# Revit family: Legrand Linkeo coffrets fixes avec panneaux latéraux fixes
name_source: partatom
category: Equipement spécialisé
units: mm (PartAtom-declared; Revit-internal decimal feet)

## family parameters
Basée sur le plan de construction = Non
Cote de connecteur circulaire = Utiliser le diamètre
Couper avec des vides une fois chargée = Non
Numéro OmniClass = 23.80.30.11.17
Partagée = Oui
Point de calcul de pièce = Non
Titre OmniClass = Distribution Boards and Control Panels
Toujours verticalement = Oui
Type d'élément = Normal

## types (12) — shared parameters
Avec mise à la terre = Oui
Avec parois latérales = Oui
Avec porte frontale = Oui
Avec tôle de toit = Oui
Classe d'application = Coffrets Legrand
Couleur = gris
Dimension modulaire = 482.6 mm (19 pouces)
Démontable = Oui
Emplacement de rack = 40 mm
Epaisseur (mm) = 1.5 mm  [stored 0.00492126 ft]
Fabricant = Legrand
Finition de surface = Poudré
Finition du rail profilé = En forme de L
Fixation X = 400 mm  [stored 1.31234 ft]
Fonction = Coffrets fixes Linkeo Legrand
Indice de protection IK = IK08
Indice de protection IP = IP20
Largeur (mm) = 605 mm  [stored 1.98491 ft]
Lien e-catalogue = https://www.legrand.fr
Matériau = Acier
Modèle = Corps fixe
Nombre de portes = 1
Passage utile en largeur (mm) = 526 mm  [stored 1.72572 ft]
RAL = 7016
Type d'aération = Passif
Type de montage = Frontal
zero-valued in all types: Elévation par défaut

## per-type parameters (varying)
| type | Capacité de charge max | EAN | Fixation Y | Hauteur (mm) | Nombre d'unités en hauteur | Passage utile en hauteur (mm) | Profondeur (mm) | Référence Legrand |
| Coffret fixe Legrand Linkeo 12U W600 D450 646202.rfa | 36 | 3414970967794 | 419 mm | 625 mm | 12 | 555 mm | 454 mm  [stored 1.4895 ft] | 646202 |
| Coffret fixe Legrand Linkeo 12U W600 D600 646212.rfa | 36 | 3414970967855 | 419 mm | 625 mm | 12 | 555 mm | 604 mm  [stored 1.98163 ft] | 646212 |
| Coffret fixe Legrand Linkeo 15U W600 D450 646203.rfa | 45 | 3414970967800 | 552 mm | 759 mm | 15 | 688 mm | 454 mm  [stored 1.4895 ft] | 646203 |
| Coffret fixe Legrand Linkeo 15U W600 D600 646213.rfa | 45 | 3414970967862 | 552 mm | 759 mm | 15 | 688 mm | 604 mm  [stored 1.98163 ft] | 646213 |
| Coffret fixe Legrand Linkeo 18U W600 D450 646204.rfa | 54 | 3414970967817 | 685 mm | 892 mm | 18 | 821 mm | 454 mm  [stored 1.4895 ft] | 646204 |
| Coffret fixe Legrand Linkeo 18U W600 D600 646214.rfa | 54 | 3414970967879 | 685 mm | 892 mm | 18 | 821 mm | 604 mm  [stored 1.98163 ft] | 646214 |
| Coffret fixe Legrand Linkeo 21U W600 D450 646205.rfa | 63 | 3414970967824 | 819 mm  [stored 2.68701 ft] | 1025 mm  [stored 3.36286 ft] | 21 | 955 mm  [stored 3.1332 ft] | 454 mm  [stored 1.4895 ft] | 646205 |
| Coffret fixe Legrand Linkeo 21U W600 D600 646215.rfa | 63 | 3414970967886 | 819 mm  [stored 2.68701 ft] | 1025 mm  [stored 3.36286 ft] | 21 | 955 mm  [stored 3.1332 ft] | 604 mm  [stored 1.98163 ft] | 646215 |
| Coffret fixe Legrand Linkeo 6U W600 D450 646200.rfa | 18 | 3414970967770 | 152 mm | 359 mm | 6 | 288 mm | 454 mm  [stored 1.4895 ft] | 646200 |
| Coffret fixe Legrand Linkeo 6U W600 D600 646210.rfa | 18 | 3414970967831 | 152 mm | 359 mm | 6 | 288 mm | 604 mm  [stored 1.98163 ft] | 646210 |
| Coffret fixe Legrand Linkeo 9U W600 D450 646201.rfa | 27 | 3414970967787 | 286 mm | 492 mm | 9 | 422 mm | 454 mm  [stored 1.4895 ft] | 646201 |
| Coffret fixe Legrand Linkeo 9U W600 D600 646211.rfa | 27 | 3414970967848 | 286 mm | 492 mm | 9 | 422 mm | 604 mm  [stored 1.98163 ft] | 646211 |

note: column(s) folded — value = type name in every type: Libellé BIM

note: [stored X ft] marks values corroborated as IEEE doubles in the binary element streams (Revit-internal decimal feet)
